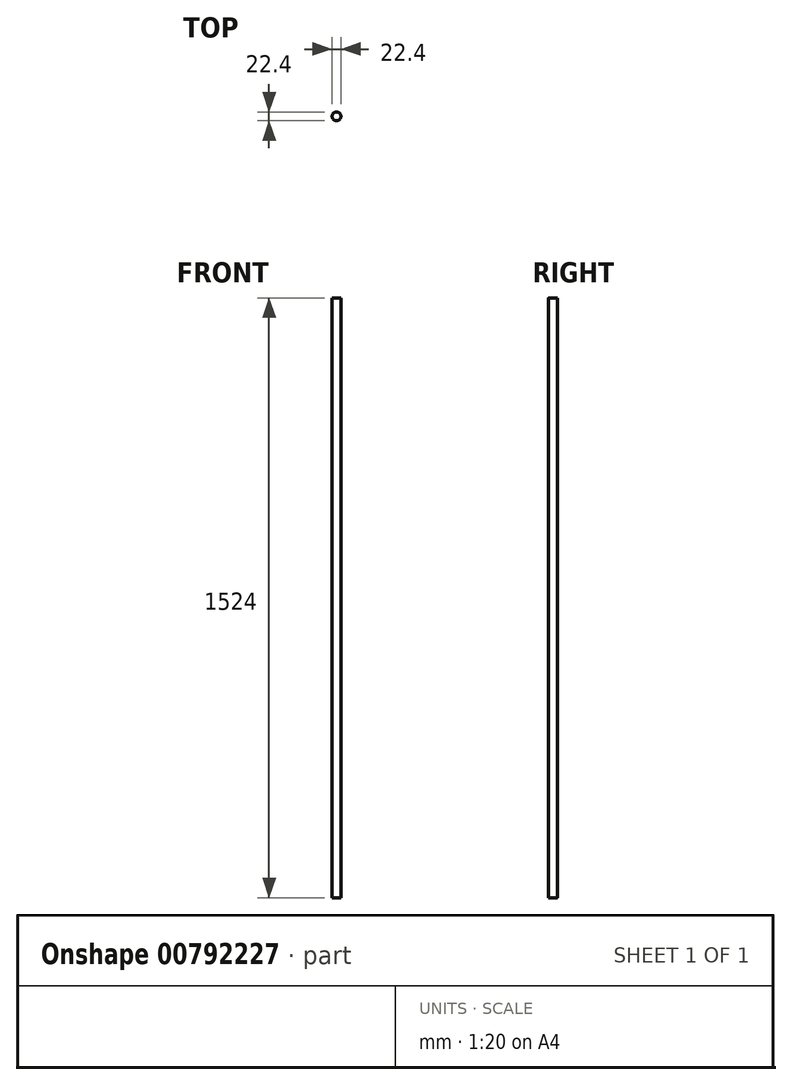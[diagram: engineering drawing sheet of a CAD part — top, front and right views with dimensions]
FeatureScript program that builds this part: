
annotation { "Feature Type Name" : "Feature", "Feature Type Description" : "" }
export const myFeature = defineFeature(function(context is Context, id is Id, definition is map)
    precondition{}
    {
        {
            var Q0;
            Q0=qCreatedBy(makeId("Top.planeOp"),FACE);
            var sketch = newSketch(context, id + "F0", { "sketchPlane" : qUnion([Q0])});
            skCircle(sketch, "E0", {"center": v(0, 0) * mm, "radius": 11.2 * mm});
            skSolve(sketch);
        }
        {
            var Q0;
            Q0 = qSketchRegion(id + "F0", true);
            extrude(context, id + "F1", {"entities" : qUnion([Q0]), "depth" : 1524 * mm, "offsetDistance" : 25.4 * mm});
        }
    });
